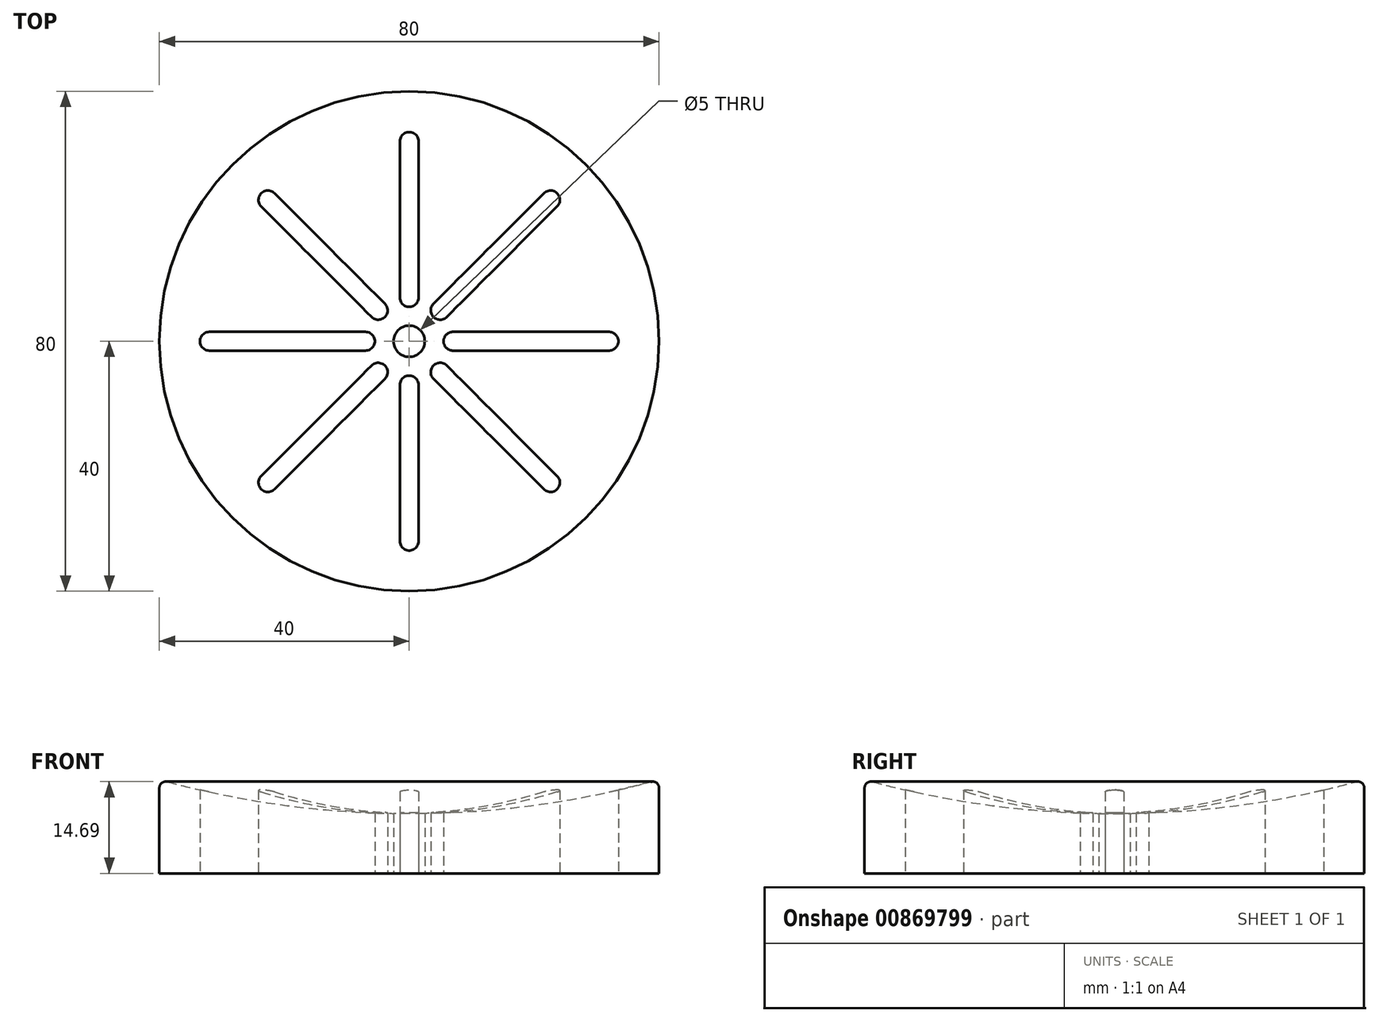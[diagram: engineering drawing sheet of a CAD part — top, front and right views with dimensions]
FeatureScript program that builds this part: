
annotation { "Feature Type Name" : "Feature", "Feature Type Description" : "" }
export const myFeature = defineFeature(function(context is Context, id is Id, definition is map)
    precondition{}
    {
        {
            var Q0;
            Q0=qCreatedBy(makeId("Top.planeOp"),FACE);
            var sketch = newSketch(context, id + "F0", { "sketchPlane" : qUnion([Q0])});
            skCircle(sketch, "E0", {"center": v(0, 0) * mm, "radius": 40 * mm});
            skSolve(sketch);
        }
        {
            var Q0;
            Q0=makeQuery(id+"F0.imprint","IMPRINT",FACE,{"disambiguationData":[TD([[makeQuery(id+"F0.imprint","IMPRINT",EDGE,{"derivedFrom":sQuery(id+"F0.wireOp",EDGE,"E0")}),1.0]])]});
            extrude(context, id + "F1", {"entities" : qUnion([Q0]), "depth" : 15 * mm, "offsetDistance" : 25 * mm});
        }
        {
            var Q0;
            Q0=qCreatedBy(makeId("Front.planeOp"),FACE);
            var sketch = newSketch(context, id + "F2", { "sketchPlane" : qUnion([Q0])});
            skArc(sketch, "E1", {"start": v(0, 9.57) * mm, "mid": v(20.18, 10.93) * mm, "end": v(40, 15) * mm});
            skLineSegment(sketch, "E2.0.0", {"start": v(0, 15) * mm, "end": v(40, 15) * mm});
            skLineSegment(sketch, "E3", {"start": v(0, 15) * mm, "end": v(0, 9.57) * mm});
            skPoint(sketch, "E4.orphan", {"position": v(-40, 15) * mm});
            skSolve(sketch);
        }
        {
            var Q0;
            Q0 = qSketchRegion(id + "F2", true);
            var Q1;
            Q1=sQuery(id+"F2.wireOp",EDGE,"E1");
            var Q2;
            Q2=sQuery(id+"F2.wireOp",EDGE,"E3");
            revolve(context, id + "F3", {"operationType" : NewBodyOperationType.REMOVE, "surfaceOperationType" : NewSurfaceOperationType.NEW, "entities" : qUnion([Q0]), "surfaceEntities" : qUnion([Q1]), "axis" : qUnion([Q2]), "revolveType" : RevolveType.FULL, "oppositeDirection" : true});
        }
        {
            var Q0;
            Q0=makeQuery(id+"F3.boolean.opBoolean","COPY",FACE,{"derivedFrom":makeQuery(id+"F3.opRevolve","SWEPT_FACE",FACE,{"disambiguationData":[OSD([sQuery(id+"F2.wireOp",EDGE,"E1")])]})});
            fillet(context, id + "F4", {"entities" : qUnion([Q0]), "radius" : 1 * mm, "tangentPropagation" : true, "allowEdgeOverflow" : false});
        }
        {
            var Q0;
            Q0=qCreatedBy(makeId("Top.planeOp"),FACE);
            var sketch = newSketch(context, id + "F5", { "sketchPlane" : qUnion([Q0])});
            skCircle(sketch, "E5", {"center": v(0, 0) * mm, "radius": 2.5 * mm});
            skArc(sketch, "E6", {"start": v(-7, -1.5) * mm, "mid": v(-5.5, 0) * mm, "end": v(-7, 1.5) * mm});
            skArc(sketch, "E7", {"start": v(-32, 1.5) * mm, "mid": v(-33.5, 0) * mm, "end": v(-32, -1.5) * mm});
            skLineSegment(sketch, "E8", {"start": v(-7, -1.5) * mm, "end": v(-32, -1.5) * mm});
            skLineSegment(sketch, "E9", {"start": v(-7, 1.5) * mm, "end": v(-32, 1.5) * mm});
            skArc(sketch, "E10.1.0", {"start": v(-23.69, -21.57) * mm, "mid": v(-23.69, -23.69) * mm, "end": v(-21.57, -23.69) * mm});
            skLineSegment(sketch, "E10.1.1", {"start": v(-6.01, -3.89) * mm, "end": v(-23.69, -21.57) * mm});
            skLineSegment(sketch, "E10.1.2", {"start": v(-3.89, -6.01) * mm, "end": v(-21.57, -23.69) * mm});
            skArc(sketch, "E10.1.3", {"start": v(-3.89, -6.01) * mm, "mid": v(-3.89, -3.89) * mm, "end": v(-6.01, -3.89) * mm});
            skArc(sketch, "E10.2.0", {"start": v(-1.5, -32) * mm, "mid": v(0, -33.5) * mm, "end": v(1.5, -32) * mm});
            skLineSegment(sketch, "E10.2.1", {"start": v(-1.5, -7) * mm, "end": v(-1.5, -32) * mm});
            skLineSegment(sketch, "E10.2.2", {"start": v(1.5, -7) * mm, "end": v(1.5, -32) * mm});
            skArc(sketch, "E10.2.3", {"start": v(1.5, -7) * mm, "mid": v(0, -5.5) * mm, "end": v(-1.5, -7) * mm});
            skArc(sketch, "E10.3.0", {"start": v(21.57, -23.69) * mm, "mid": v(23.69, -23.69) * mm, "end": v(23.69, -21.57) * mm});
            skLineSegment(sketch, "E10.3.1", {"start": v(3.89, -6.01) * mm, "end": v(21.57, -23.69) * mm});
            skLineSegment(sketch, "E10.3.2", {"start": v(6.01, -3.89) * mm, "end": v(23.69, -21.57) * mm});
            skArc(sketch, "E10.3.3", {"start": v(6.01, -3.89) * mm, "mid": v(3.89, -3.89) * mm, "end": v(3.89, -6.01) * mm});
            skArc(sketch, "E10.4.0", {"start": v(32, -1.5) * mm, "mid": v(33.5, 0) * mm, "end": v(32, 1.5) * mm});
            skLineSegment(sketch, "E10.4.1", {"start": v(7, -1.5) * mm, "end": v(32, -1.5) * mm});
            skLineSegment(sketch, "E10.4.2", {"start": v(7, 1.5) * mm, "end": v(32, 1.5) * mm});
            skArc(sketch, "E10.4.3", {"start": v(7, 1.5) * mm, "mid": v(5.5, 0) * mm, "end": v(7, -1.5) * mm});
            skArc(sketch, "E10.5.0", {"start": v(23.69, 21.57) * mm, "mid": v(23.69, 23.69) * mm, "end": v(21.57, 23.69) * mm});
            skLineSegment(sketch, "E10.5.1", {"start": v(6.01, 3.89) * mm, "end": v(23.69, 21.57) * mm});
            skLineSegment(sketch, "E10.5.2", {"start": v(3.89, 6.01) * mm, "end": v(21.57, 23.69) * mm});
            skArc(sketch, "E10.5.3", {"start": v(3.89, 6.01) * mm, "mid": v(3.89, 3.89) * mm, "end": v(6.01, 3.89) * mm});
            skArc(sketch, "E10.6.0", {"start": v(1.5, 32) * mm, "mid": v(0, 33.5) * mm, "end": v(-1.5, 32) * mm});
            skLineSegment(sketch, "E10.6.1", {"start": v(1.5, 7) * mm, "end": v(1.5, 32) * mm});
            skLineSegment(sketch, "E10.6.2", {"start": v(-1.5, 7) * mm, "end": v(-1.5, 32) * mm});
            skArc(sketch, "E10.6.3", {"start": v(-1.5, 7) * mm, "mid": v(0, 5.5) * mm, "end": v(1.5, 7) * mm});
            skArc(sketch, "E10.7.0", {"start": v(-21.57, 23.69) * mm, "mid": v(-23.69, 23.69) * mm, "end": v(-23.69, 21.57) * mm});
            skLineSegment(sketch, "E10.7.1", {"start": v(-3.89, 6.01) * mm, "end": v(-21.57, 23.69) * mm});
            skLineSegment(sketch, "E10.7.2", {"start": v(-6.01, 3.89) * mm, "end": v(-23.69, 21.57) * mm});
            skArc(sketch, "E10.7.3", {"start": v(-6.01, 3.89) * mm, "mid": v(-3.89, 3.89) * mm, "end": v(-3.89, 6.01) * mm});
            skSolve(sketch);
        }
        {
            var Q0;
            Q0 = qSketchRegion(id + "F5", true);
            extrude(context, id + "F6", {"entities" : qUnion([Q0]), "operationType" : NewBodyOperationType.REMOVE, "endBound" : BoundingType.THROUGH_ALL, "depth" : 25 * mm, "offsetDistance" : 25 * mm});
        }
    });
